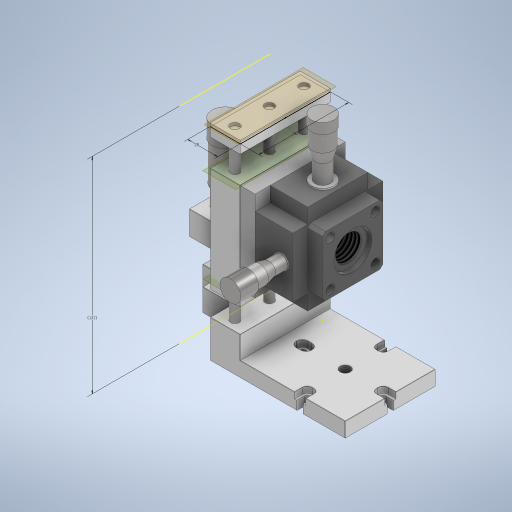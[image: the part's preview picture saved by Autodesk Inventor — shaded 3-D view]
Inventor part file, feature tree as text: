
AUTODESK INVENTOR PART (.ipt)
format: ipt  version: 2023.5 (Build 275446000, 446)  size: 927,744 bytes
history: native  units: mm
features: sketch x33, extrude x20, plane x8, revolve x4, hole x4, chamfer x2, fillet x1, thread x1
ambient origin geometry x8: Origin, YZ Plane, XZ Plane, XY Plane, X Axis, Y Axis, Z Axis, Center Point
bodies: 实体1 (feature_tree)
feature tree (73):
  extrude  "拉伸1"  Depth=60.0mm
  extrude  "拉伸2"  Depth=10.0mm
  extrude  "拉伸3"  Depth=10.0mm TaperAngle=0.0deg
  plane  "工作平面1"
  extrude  "拉伸4"  Depth=15.0mm
  extrude  "拉伸5"  Depth=20.0mm TaperAngle=0.0deg
  extrude  "拉伸6"  Depth=15.0mm
  extrude  "拉伸7"  Depth=7.5mm
  sketch  "草图10"  dims[d17=26.0mm d18=0.0mm d19=25.0mm d20=0.0mm]
  plane  "工作平面2"
  extrude  "拉伸9"  Depth=25.0mm TaperAngle=0.0deg
  plane  "工作平面3"
  extrude  "拉伸10"  Depth=0.2mm TaperAngle=0.0deg
  extrude  "拉伸12"  Depth=23.0mm
  extrude  "拉伸13"  Depth=5.8mm
  extrude  "拉伸15"  Depth=5.8mm
  extrude  "拉伸16"  Depth=70.0mm TaperAngle=0.0deg
  extrude  "拉伸17"  Depth=15.0mm
  plane  "工作平面5"
  revolve  "旋转1"  [1 undecoded]
  plane  "工作平面6"
  revolve  "旋转2"  [1 undecoded]
  plane  "工作平面7"
  revolve  "旋转3"  [1 undecoded]
  sketch  "草图23"  dims[d59=0.01mm d60=0.0mm d61=10.0mm]
  plane  "工作平面8"
  extrude  "拉伸18"  Depth=60.0mm TaperAngle=0.0deg
  hole  "孔2"  [1 undecoded]
  sketch  "草图29"  dims[d67=40.0mm d68=40.0mm d69=10.0mm d70=0.0mm]
  hole  "孔3"  [1 undecoded]
  hole  "孔4"  [1 undecoded]
  sketch  "草图32"  dims[d73=5.0mm]
  hole  "孔5"  [1 undecoded]
  fillet  "圆角1"  Radius=10.0mm
  chamfer  "倒角2"  Angle=90.0deg  [1 undecoded]
  revolve  "旋转4"  [1 undecoded]
  extrude  "拉伸19"  TaperAngle=90.0deg  [1 undecoded]
  extrude  "拉伸20"  TaperAngle=90.0deg  [1 undecoded]
  sketch  "草图42"  dims[d78=0.2mm]
  plane  "工作平面9"
  sketch  "草图43"  dims[d79=7.5mm]
  extrude  "拉伸21"  Depth=10.0mm
  extrude  "拉伸22"  TaperAngle=90.0deg  [1 undecoded]
  chamfer  "倒角4"  Distance=20.0mm
  extrude  "拉伸23"  Depth=60.0mm
  thread  "螺纹1"  [1 undecoded]
  sketch  "草图1"  dims[d0=90.0mm d1=60.0mm]
  sketch  "草图2"  dims[d2=10.0mm d3=0.0mm d4=15.0mm]
  sketch  "草图3"  dims[d5=20.0mm d6=10.0mm d7=0.0mm]
  sketch  "草图5"  dims[d8=15.0mm d9=15.0mm]
  sketch  "草图7"  dims[d10=15.0mm d11=20.0mm d12=0.0mm]
  sketch  "草图8"  dims[d13=15.0mm d14=15.0mm]
  sketch  "草图9"  dims[d15=15.0mm d16=7.5mm]
  sketch  "草图11"  dims[d21=13.0mm d22=0.2mm d23=0.0mm]
  sketch  "草图12"  dims[d24=7.5mm d25=23.0mm]
  sketch  "草图14"  dims[d26=23.0mm d27=5.8mm]
  sketch  "草图15"  dims[d28=5.8mm d29=5.8mm]
  sketch  "草图17"  dims[d30=110.0mm d31=0.0mm d35=70.0mm d36=0.0mm]
  sketch  "草图18"  dims[d37=-7.5mm d38=15.0mm]
  sketch  "草图19"  dims[d39=30.0mm d40=28.0mm]
  sketch  "草图20"  dims[d41=16.0mm d42=0.0mm d46=20.0mm]
  sketch  "草图21"  dims[d47=20.0mm d48=0.01mm d49=0.0mm]
  sketch  "草图22"  dims[d50=60.0mm d51=9.99mm d52=0.0mm]
  sketch  "草图26"  dims[d62=10.0mm d63=10.0mm]
  sketch  "草图28"  dims[d64=10.0mm d65=25.0mm d66=0.0mm]
  sketch  "草图30"  dims[d71=7.5mm]
  sketch  "草图31"  dims[d72=34.0mm]
  sketch  "草图33"  dims[d74=0.5mm]
  sketch  "草图35"  dims[d75=0.5mm]
  sketch  "草图40"  dims[d76=8.0mm]
  sketch  "草图41"  dims[d77=0.1mm]
  sketch  "草图44"  dims[d80=1.0mm]
  sketch  "草图45"  dims[d81=6.0mm d82=90.0deg d83=7.5mm d84=35.0mm d85=5.0mm d86=0.5mm d87=0.5mm d88=8.0mm d94=7.5mm d95=90.0deg d96=90.0deg d97=0.5mm d98=90.0deg d109=20.0mm d110=60.0mm d111=2.0mm d112=8.0mm d113=0.0mm d114=6.0mm d115=6.0mm d116=4.0mm d117=2.0mm d118=90.0deg d119=2.0mm d120=0.0mm d121=137.0mm d122=7.0mm d124=6.9mm d125=6.4mm d126=0.9mm d127=17.4mm d128=50.7mm d129=25.0mm d130=19.0mm d131=30.0mm d132=6.0mm d133=40.0mm d135=360.0deg d137=6.0mm d138=6.0mm d139=4.0mm d140=2.0mm d141=90.0deg d142=21.7mm d143=0.0mm d144=19.0mm d145=17.294mm d146=25.0mm d147=3.023mm d148=2.0mm d149=14.3117mm d150=38.2mm d151=0.0mm d152=25.0mm d153=25.0mm d154=50.0mm d155=4.0mm d156=2.0mm d157=90.0deg d158=3.0mm d159=0.0mm d160=0.2mm d161=2.0mm d162=2.0mm d163=45.0deg d167=14.2mm d168=2.5mm d169=1.0mm d170=12.6mm d171=10.0mm d172=11.0mm d173=0.5mm d174=39.0mm d175=90.0deg d195=2.1mm d196=6.9mm d197=2.0mm d198=28.0mm d199=2.1mm d200=20.0mm d202=90.0deg d204=25.0mm d205=0.0mm d206=3.7mm d207=8.4mm d208=7.4mm d209=20.0mm d211=90.0deg d213=4.0mm d214=0.0mm d215=6.8mm d223=2.0mm d225=2.0mm d226=6.3mm d227=2.0mm d229=33.0mm d230=6.4mm d231=2.0mm d232=31.7585mm d233=10.0mm d234=0.0mm d235=10.0mm d236=7.5mm d237=3.7mm d238=4.3mm d239=0.0mm d240=0.2mm d241=2.0mm d242=45.0deg d243=10.0mm d244=0.0mm d245=10.0mm d246=0.0mm d247=4.3mm d99=0.5mm d100=0.872665mm d101=0.5mm d102=0.872665mm d103=0.25mm d104=0.375mm d105=14.3117mm d106=0.75mm d107=20.594885mm d108=0.0625mm]
note: 13 required parameter values undecoded (feature->parameter linkage not recoverable at this tier; creation-order binding heuristic only, values carry confidence <= 0.55)